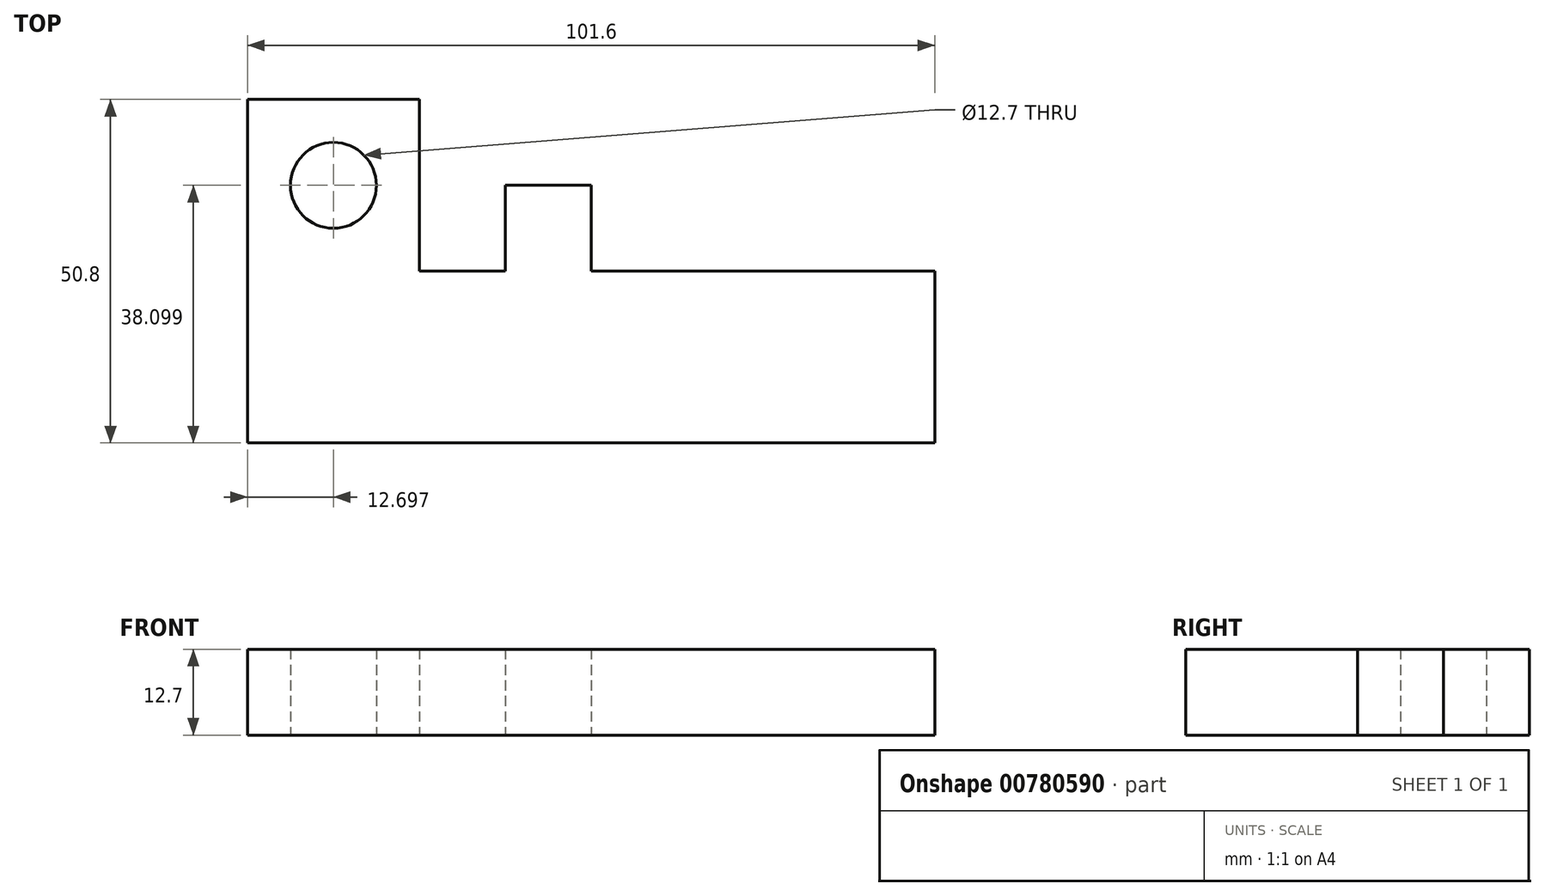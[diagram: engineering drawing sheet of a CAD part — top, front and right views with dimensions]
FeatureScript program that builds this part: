
annotation { "Feature Type Name" : "Feature", "Feature Type Description" : "" }
export const myFeature = defineFeature(function(context is Context, id is Id, definition is map)
    precondition{}
    {
        {
            var Q0;
            Q0=qCreatedBy(makeId("Top.planeOp"),FACE);
            var sketch = newSketch(context, id + "F0", { "sketchPlane" : qUnion([Q0])});
            skLineSegment(sketch, "E0", {"start": v(-36.47, 20.2) * mm, "end": v(-36.47, -30.6) * mm});
            skLineSegment(sketch, "E1", {"start": v(-36.47, -30.6) * mm, "end": v(65.13, -30.6) * mm});
            skLineSegment(sketch, "E2", {"start": v(65.13, -30.6) * mm, "end": v(65.13, -5.2) * mm});
            skLineSegment(sketch, "E3", {"start": v(65.13, -5.2) * mm, "end": v(14.33, -5.2) * mm});
            skLineSegment(sketch, "E4", {"start": v(14.33, -5.2) * mm, "end": v(14.33, 7.5) * mm});
            skLineSegment(sketch, "E5", {"start": v(14.33, 7.5) * mm, "end": v(1.63, 7.5) * mm});
            skLineSegment(sketch, "E6", {"start": v(1.63, 7.5) * mm, "end": v(1.63, -5.2) * mm});
            skLineSegment(sketch, "E7", {"start": v(1.63, -5.2) * mm, "end": v(-11.07, -5.2) * mm});
            skLineSegment(sketch, "E8", {"start": v(-11.07, -5.2) * mm, "end": v(-11.07, 20.2) * mm});
            skLineSegment(sketch, "E9", {"start": v(-11.07, 20.2) * mm, "end": v(-36.47, 20.2) * mm});
            skLineSegment(sketch, "E10", {"start": v(-23.77, 20.2) * mm, "end": v(-23.77, -30.6) * mm, "construction": true});
            skLineSegment(sketch, "E11", {"start": v(-11.07, 7.5) * mm, "end": v(-36.47, 7.5) * mm, "construction": true});
            skCircle(sketch, "E12", {"center": v(-23.77, 7.5) * mm, "radius": 6.35 * mm});
            skSolve(sketch);
        }
        {
            var Q0;
            Q0 = qSketchRegion(id + "F0", true);
            extrude(context, id + "F1", {"entities" : qUnion([Q0]), "depth" : 12.7 * mm, "offsetDistance" : 25.4 * mm});
        }
    });
